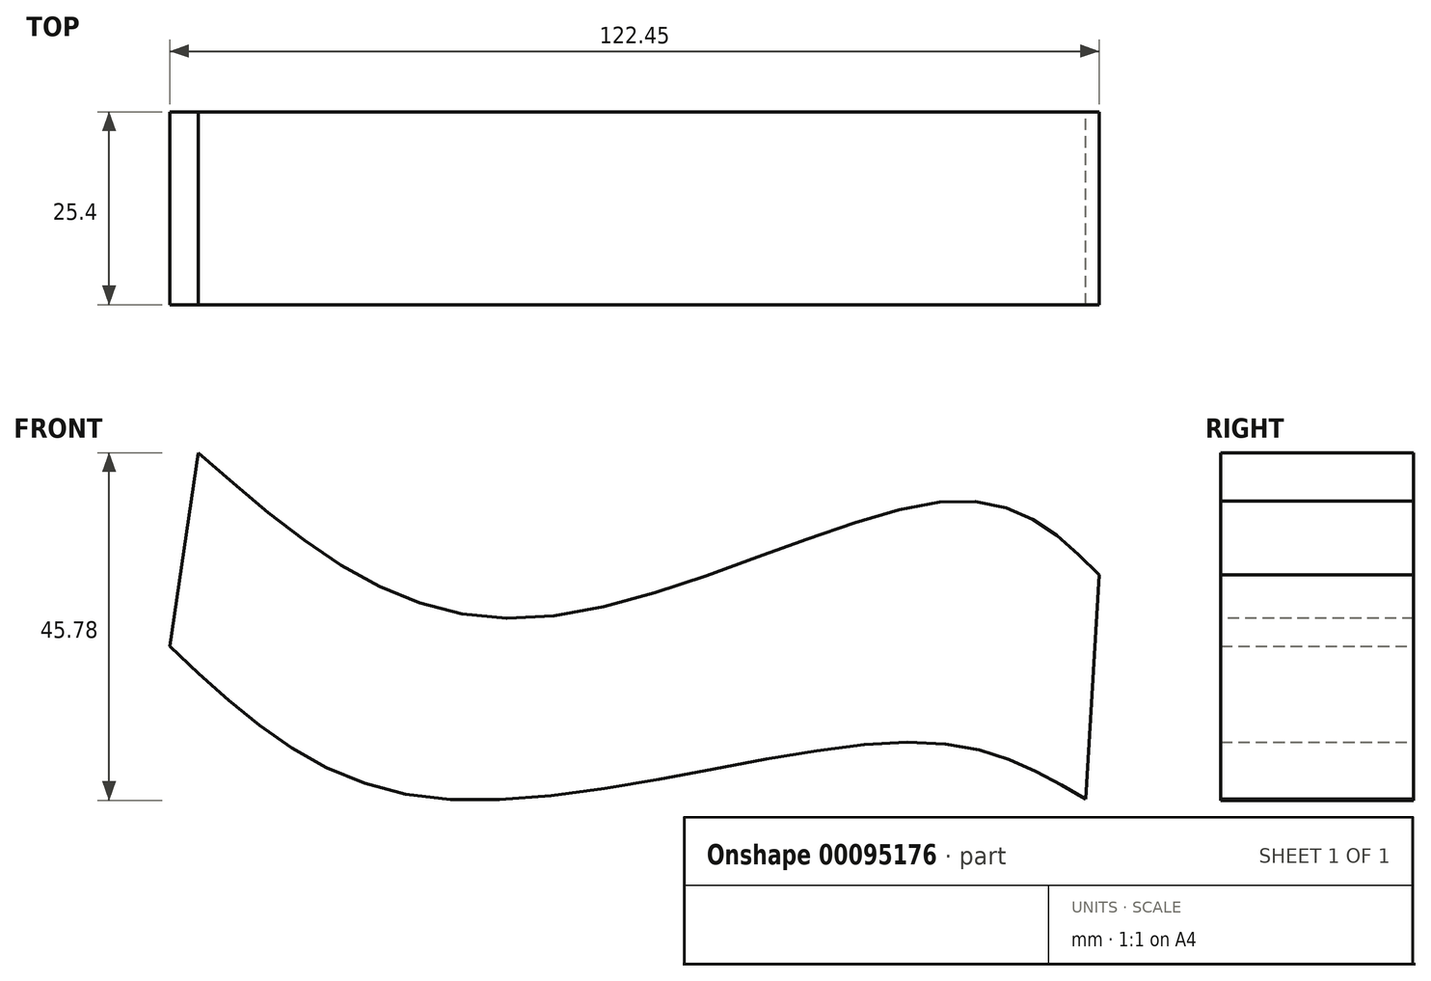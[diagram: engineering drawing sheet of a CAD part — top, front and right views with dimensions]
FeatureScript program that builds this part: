
annotation { "Feature Type Name" : "Feature", "Feature Type Description" : "" }
export const myFeature = defineFeature(function(context is Context, id is Id, definition is map)
    precondition{}
    {
        {
            var Q0;
            Q0=qCreatedBy(makeId("Front.planeOp"),FACE);
            var sketch = newSketch(context, id + "F0", { "sketchPlane" : qUnion([Q0])});
            skFitSpline(sketch, "E0", {"points": [v(-47.43, 25.5) * mm, v(-5.36, 3.67) * mm, v(52.8, 19.15) * mm, v(71.25, 9.43) * mm], "startDerivative": vector(105.2, -92.76) * mm, "endDerivative": vector(62.78, -62.23) * mm});
            skFitSpline(sketch, "E1", {"points": [v(-51.2, 0) * mm, v(-17.07, -19.95) * mm, v(46.64, -12.6) * mm, v(69.46, -20.14) * mm], "startDerivative": vector(87.81, -83.33) * mm, "endDerivative": vector(73.37, -43.9) * mm});
            skLineSegment(sketch, "E2", {"start": v(-47.43, 25.5) * mm, "end": v(-51.2, 0) * mm});
            skLineSegment(sketch, "E3", {"start": v(71.25, 9.43) * mm, "end": v(69.46, -20.14) * mm});
            skSolve(sketch);
        }
        {
            var Q0;
            Q0 = qSketchRegion(id + "F0", true);
            extrude(context, id + "F1", {"entities" : qUnion([Q0]), "endBound" : BoundingType.SYMMETRIC, "depth" : 25.4 * mm});
        }
    });
